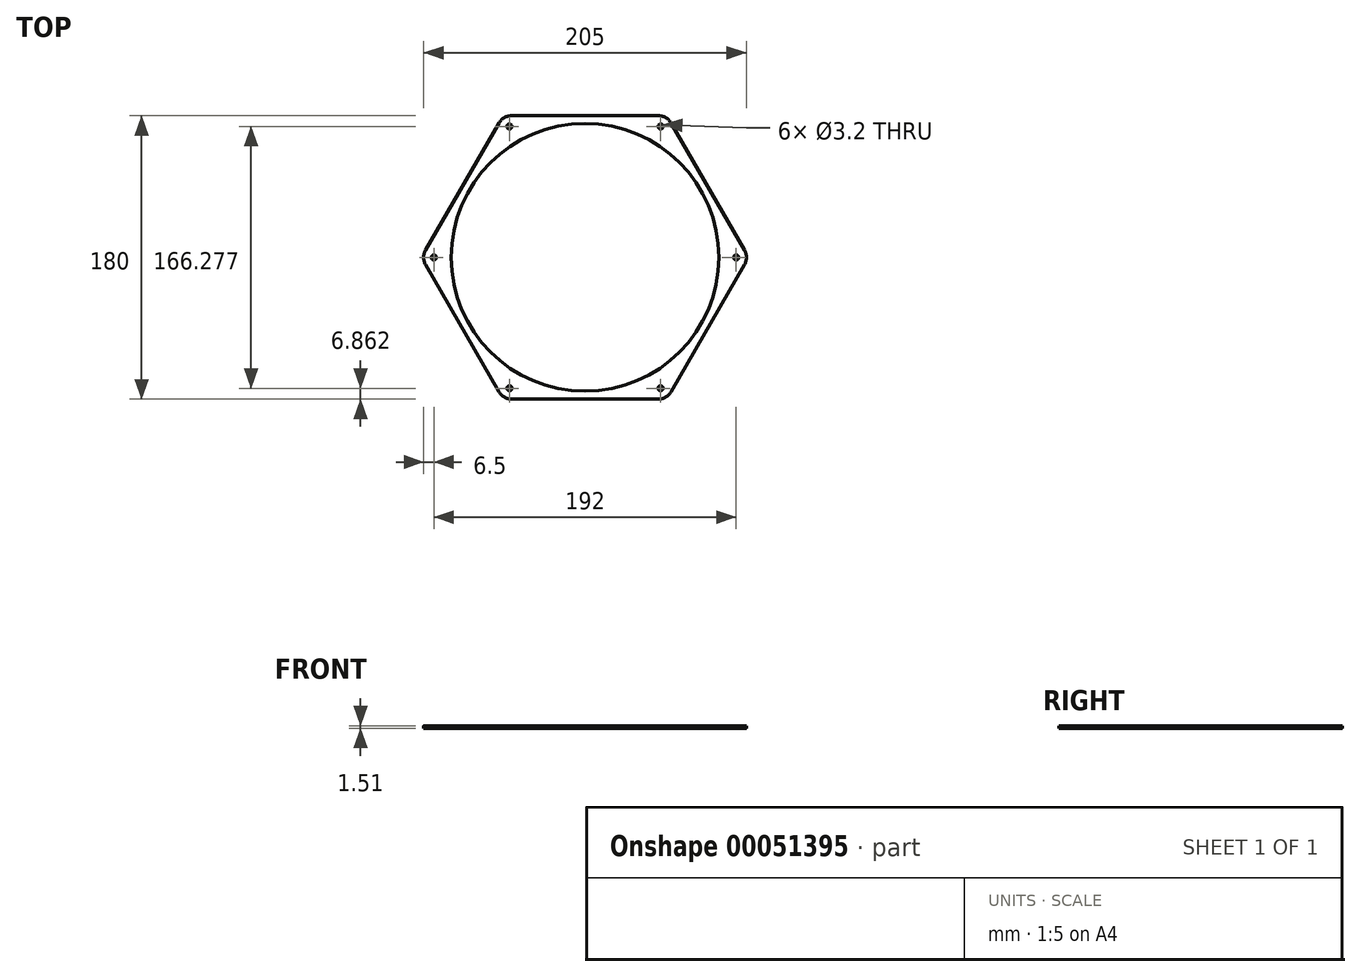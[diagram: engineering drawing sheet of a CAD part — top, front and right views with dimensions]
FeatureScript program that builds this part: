
annotation { "Feature Type Name" : "Feature", "Feature Type Description" : "" }
export const myFeature = defineFeature(function(context is Context, id is Id, definition is map)
    precondition{}
    {
        {
            var Q0;
            Q0=qCreatedBy(makeId("Top.planeOp"),FACE);
            var sketch = newSketch(context, id + "F0", { "sketchPlane" : qUnion([Q0])});
            skCircle(sketch, "E0.cCircle", {"center": v(0, 0) * mm, "radius": 90 * mm, "construction": true});
            skLineSegment(sketch, "E0.0", {"start": v(-51.96, 90) * mm, "end": v(51.96, 90) * mm});
            skLineSegment(sketch, "E0.1", {"start": v(51.96, 90) * mm, "end": v(103.92, 0) * mm});
            skLineSegment(sketch, "E0.2", {"start": v(103.92, 0) * mm, "end": v(51.96, -90) * mm});
            skLineSegment(sketch, "E0.3", {"start": v(51.96, -90) * mm, "end": v(-51.96, -90) * mm});
            skLineSegment(sketch, "E0.4", {"start": v(-51.96, -90) * mm, "end": v(-103.92, 0) * mm});
            skLineSegment(sketch, "E0.5", {"start": v(-103.92, 0) * mm, "end": v(-51.96, 90) * mm});
            skPoint(sketch, "E0.0.midPoint", {"position": v(0, 90) * mm});
            skSolve(sketch);
        }
        {
            var Q0;
            Q0=makeQuery(id+"F0.imprint","IMPRINT",FACE,{"disambiguationData":[TD([[makeQuery(id+"F0.imprint","IMPRINT",EDGE,{"derivedFrom":sQuery(id+"F0.wireOp",EDGE,"E0.0")}),-1.0]])]});
            extrude(context, id + "F1", {"entities" : qUnion([Q0]), "depth" : 1.5 * mm});
        }
        {
            var Q0;
            Q0=makeQuery(id+"F1.opExtrude","SWEPT_EDGE",EDGE,{"disambiguationData":[OSD([sQuery(id+"F0.wireOp",EDGE,"E0.4"),sQuery(id+"F0.wireOp",EDGE,"E0.5")])]});
            var Q1;
            Q1=makeQuery(id+"F1.opExtrude","SWEPT_EDGE",EDGE,{"disambiguationData":[OSD([sQuery(id+"F0.wireOp",EDGE,"E0.0"),sQuery(id+"F0.wireOp",EDGE,"E0.5")])]});
            var Q2;
            Q2=makeQuery(id+"F1.opExtrude","SWEPT_EDGE",EDGE,{"disambiguationData":[OSD([sQuery(id+"F0.wireOp",EDGE,"E0.0"),sQuery(id+"F0.wireOp",EDGE,"E0.1")])]});
            var Q3;
            Q3=makeQuery(id+"F1.opExtrude","SWEPT_EDGE",EDGE,{"disambiguationData":[OSD([sQuery(id+"F0.wireOp",EDGE,"E0.1"),sQuery(id+"F0.wireOp",EDGE,"E0.2")])]});
            var Q4;
            Q4=makeQuery(id+"F1.opExtrude","SWEPT_EDGE",EDGE,{"disambiguationData":[OSD([sQuery(id+"F0.wireOp",EDGE,"E0.2"),sQuery(id+"F0.wireOp",EDGE,"E0.3")])]});
            var Q5;
            Q5=makeQuery(id+"F1.opExtrude","SWEPT_EDGE",EDGE,{"disambiguationData":[OSD([sQuery(id+"F0.wireOp",EDGE,"E0.3"),sQuery(id+"F0.wireOp",EDGE,"E0.4")])]});
            fillet(context, id + "F2", {"entities" : qUnion([Q0, Q1, Q2, Q3, Q4, Q5]), "radius" : 9.2 * mm, "tangentPropagation" : true, "allowEdgeOverflow" : false});
        }
        {
            var Q0;
            Q0=makeQuery(id+"F1.opExtrude","CAP_FACE",FACE,{"disambiguationData":[OSD([sQuery(id+"F0.wireOp",EDGE,"E0.0"),sQuery(id+"F0.wireOp",EDGE,"E0.1"),sQuery(id+"F0.wireOp",EDGE,"E0.2"),sQuery(id+"F0.wireOp",EDGE,"E0.3"),sQuery(id+"F0.wireOp",EDGE,"E0.4"),sQuery(id+"F0.wireOp",EDGE,"E0.5")])],"isStart":false});
            var sketch = newSketch(context, id + "F3", { "sketchPlane" : qUnion([Q0])});
            skCircle(sketch, "E1", {"center": v(0, 0) * mm, "radius": 85 * mm});
            skSolve(sketch);
        }
        {
            var Q0;
            Q0 = qSketchRegion(id + "F3", true);
            extrude(context, id + "F4", {"entities" : qUnion([Q0]), "operationType" : NewBodyOperationType.ADD, "depth" : 0.01 * mm});
        }
        {
            var Q0;
            Q0=makeQuery(id+"F1.opExtrude","CAP_FACE",FACE,{"disambiguationData":[OSD([sQuery(id+"F0.wireOp",EDGE,"E0.0"),sQuery(id+"F0.wireOp",EDGE,"E0.1"),sQuery(id+"F0.wireOp",EDGE,"E0.2"),sQuery(id+"F0.wireOp",EDGE,"E0.3"),sQuery(id+"F0.wireOp",EDGE,"E0.4"),sQuery(id+"F0.wireOp",EDGE,"E0.5")])],"isStart":false});
            var sketch = newSketch(context, id + "F5", { "sketchPlane" : qUnion([Q0])});
            skLineSegment(sketch, "E2", {"start": v(0, 0) * mm, "end": v(96, 0) * mm, "construction": true});
            skCircle(sketch, "E3", {"center": v(96, 0) * mm, "radius": 1.6 * mm});
            skCircle(sketch, "E4.1.0", {"center": v(48, 83.14) * mm, "radius": 1.6 * mm});
            skCircle(sketch, "E4.2.0", {"center": v(-48, 83.14) * mm, "radius": 1.6 * mm});
            skCircle(sketch, "E4.3.0", {"center": v(-96, 0) * mm, "radius": 1.6 * mm});
            skCircle(sketch, "E4.4.0", {"center": v(-48, -83.14) * mm, "radius": 1.6 * mm});
            skCircle(sketch, "E4.5.0", {"center": v(48, -83.14) * mm, "radius": 1.6 * mm});
            skPoint(sketch, "E4.center", {"position": v(0, 0) * mm});
            skSolve(sketch);
        }
        {
            var Q0;
            Q0 = qSketchRegion(id + "F5", true);
            extrude(context, id + "F6", {"entities" : qUnion([Q0]), "operationType" : NewBodyOperationType.REMOVE, "endBound" : BoundingType.UP_TO_NEXT, "oppositeDirection" : true, "depth" : 25 * mm});
        }
    });
